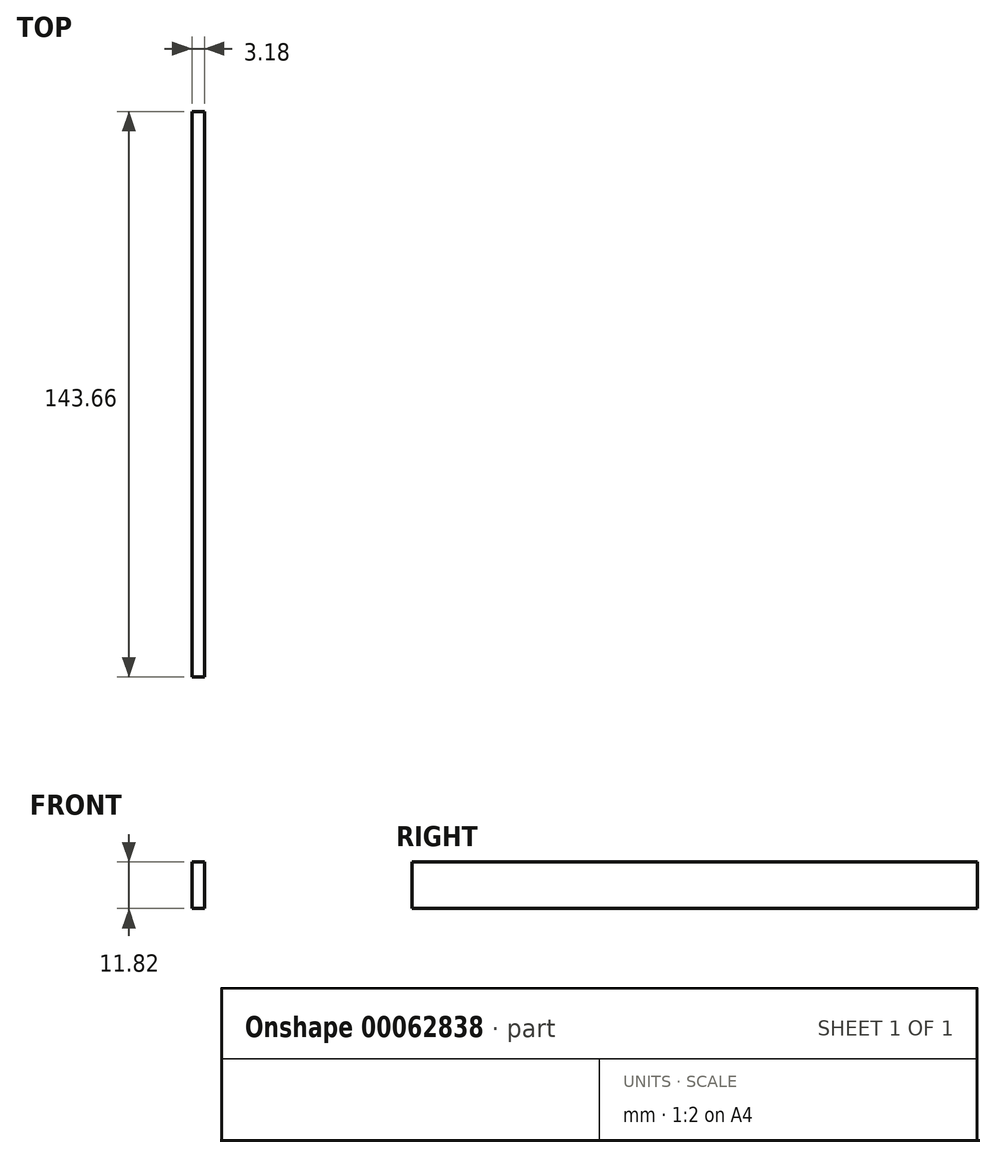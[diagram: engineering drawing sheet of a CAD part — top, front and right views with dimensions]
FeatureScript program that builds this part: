
annotation { "Feature Type Name" : "Feature", "Feature Type Description" : "" }
export const myFeature = defineFeature(function(context is Context, id is Id, definition is map)
    precondition{}
    {
        {
            var Q0;
            Q0=qCreatedBy(makeId("Right.planeOp"),FACE);
            var sketch = newSketch(context, id + "F0", { "sketchPlane" : qUnion([Q0])});
            skLineSegment(sketch, "E0.rect.bottom", {"start": v(-71.83, 5.91) * mm, "end": v(71.83, 5.91) * mm});
            skLineSegment(sketch, "E0.rect.top", {"start": v(-71.83, -5.91) * mm, "end": v(71.83, -5.91) * mm});
            skLineSegment(sketch, "E0.rect.left", {"start": v(-71.83, 5.91) * mm, "end": v(-71.83, -5.91) * mm});
            skLineSegment(sketch, "E0.rect.right", {"start": v(71.83, 5.91) * mm, "end": v(71.83, -5.91) * mm});
            skPoint(sketch, "E0.rect.middle", {"position": v(0, 0) * mm});
            skSolve(sketch);
        }
        {
            var Q0;
            Q0=makeQuery(id+"F0.imprint","IMPRINT",FACE,{"disambiguationData":[TD([[makeQuery(id+"F0.imprint","IMPRINT",EDGE,{"derivedFrom":sQuery(id+"F0.wireOp",EDGE,"E0.rect.bottom")}),-1.0]])]});
            extrude(context, id + "F1", {"entities" : qUnion([Q0]), "endBound" : BoundingType.SYMMETRIC, "depth" : 3.17 * mm});
        }
    });
